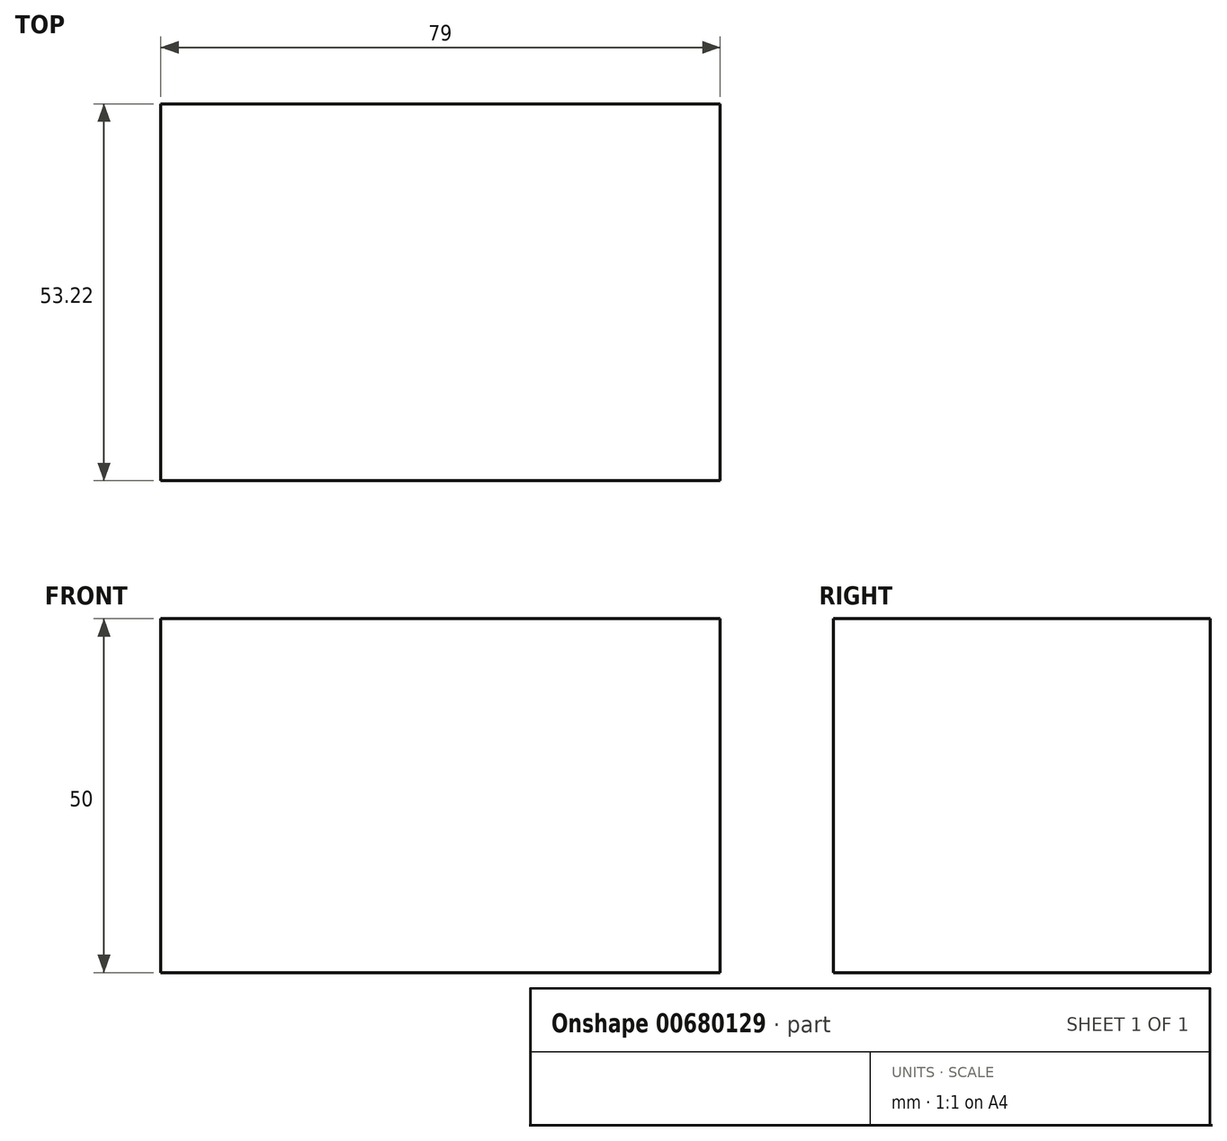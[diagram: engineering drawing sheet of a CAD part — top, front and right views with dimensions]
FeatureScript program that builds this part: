
annotation { "Feature Type Name" : "Feature", "Feature Type Description" : "" }
export const myFeature = defineFeature(function(context is Context, id is Id, definition is map)
    precondition{}
    {
        {
            var Q0;
            Q0=qCreatedBy(makeId("Top.planeOp"),FACE);
            var sketch = newSketch(context, id + "F0", { "sketchPlane" : qUnion([Q0])});
            skLineSegment(sketch, "E0.bottom", {"start": v(39.5, -26.61) * mm, "end": v(-39.5, -26.61) * mm});
            skLineSegment(sketch, "E0.top", {"start": v(39.5, 26.61) * mm, "end": v(-39.5, 26.61) * mm});
            skLineSegment(sketch, "E0.left", {"start": v(39.5, -26.61) * mm, "end": v(39.5, 26.61) * mm});
            skLineSegment(sketch, "E0.right", {"start": v(-39.5, -26.61) * mm, "end": v(-39.5, 26.61) * mm});
            skPoint(sketch, "E0.middle", {"position": v(0, 0) * mm});
            skSolve(sketch);
        }
        {
            var Q0;
            Q0=makeQuery(id+"F0.imprint","IMPRINT",FACE,{"disambiguationData":[TD([[makeQuery(id+"F0.imprint","IMPRINT",EDGE,{"derivedFrom":sQuery(id+"F0.wireOp",EDGE,"E0.bottom")}),-1.0]])]});
            extrude(context, id + "F1", {"entities" : qUnion([Q0]), "depth" : 50 * mm, "offsetDistance" : 25 * mm});
        }
    });
